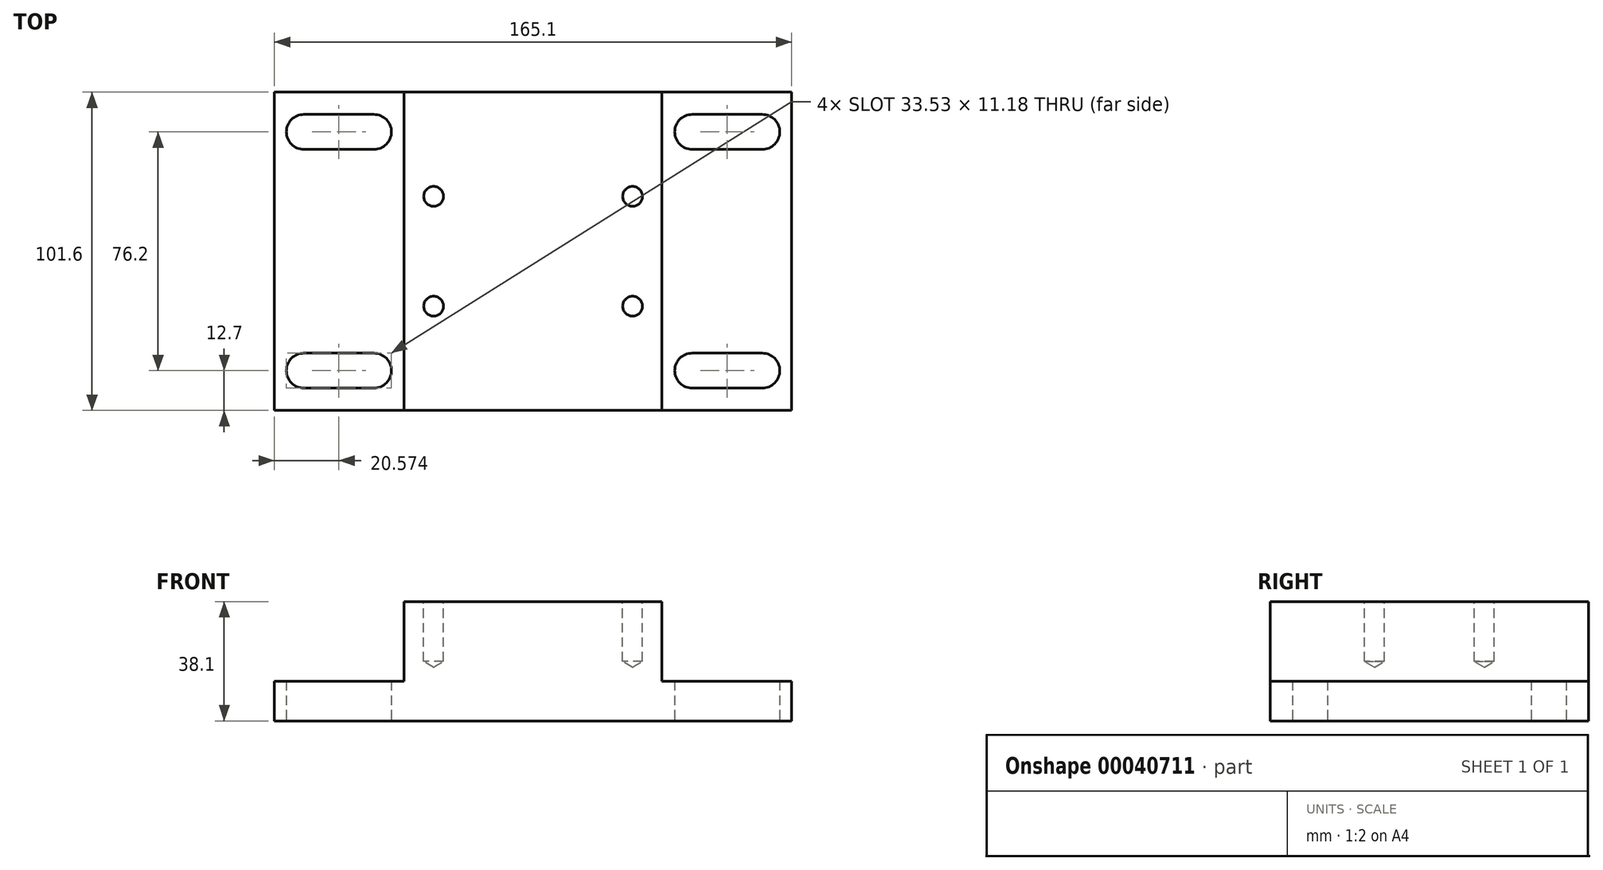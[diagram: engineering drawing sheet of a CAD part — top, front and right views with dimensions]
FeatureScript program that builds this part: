
annotation { "Feature Type Name" : "Feature", "Feature Type Description" : "" }
export const myFeature = defineFeature(function(context is Context, id is Id, definition is map)
    precondition{}
    {
        {
            var Q0;
            Q0=qCreatedBy(makeId("Top.planeOp"),FACE);
            var sketch = newSketch(context, id + "F0", { "sketchPlane" : qUnion([Q0])});
            skLineSegment(sketch, "E0.rect.bottom", {"start": v(-82.55, 50.8) * mm, "end": v(82.55, 50.8) * mm});
            skLineSegment(sketch, "E0.rect.top", {"start": v(-82.55, -50.8) * mm, "end": v(82.55, -50.8) * mm});
            skLineSegment(sketch, "E0.rect.left", {"start": v(-82.55, 50.8) * mm, "end": v(-82.55, -50.8) * mm});
            skLineSegment(sketch, "E0.rect.right", {"start": v(82.55, 50.8) * mm, "end": v(82.55, -50.8) * mm});
            skPoint(sketch, "E0.rect.middle", {"position": v(0, 0) * mm});
            skLineSegment(sketch, "E1", {"start": v(0, 50.8) * mm, "end": v(0, -50.8) * mm, "construction": true});
            skLineSegment(sketch, "E2", {"start": v(-82.55, 0) * mm, "end": v(82.55, 0) * mm, "construction": true});
            skLineSegment(sketch, "E3.0", {"start": v(-82.55, 38.1) * mm, "end": v(82.55, 38.1) * mm, "construction": true});
            skLineSegment(sketch, "E4.0", {"start": v(-61.98, 50.8) * mm, "end": v(-61.98, -50.8) * mm, "construction": true});
            skLineSegment(sketch, "E5.0", {"start": v(-73.15, 50.8) * mm, "end": v(-73.15, -50.8) * mm, "construction": true});
            skLineSegment(sketch, "E6.0", {"start": v(-50.8, 50.8) * mm, "end": v(-50.8, -50.8) * mm, "construction": true});
            skLineSegment(sketch, "E7", {"start": v(-73.15, 38.1) * mm, "end": v(-50.8, 38.1) * mm});
            skArc(sketch, "E8.0.startCap", {"start": v(-73.15, 32.51) * mm, "mid": v(-78.74, 38.1) * mm, "end": v(-73.15, 43.69) * mm});
            skArc(sketch, "E8.0.endCap", {"start": v(-50.8, 43.69) * mm, "mid": v(-45.21, 38.1) * mm, "end": v(-50.8, 32.51) * mm});
            skLineSegment(sketch, "E8.0.left", {"start": v(-73.15, 43.69) * mm, "end": v(-50.8, 43.69) * mm});
            skLineSegment(sketch, "E8.0.right", {"start": v(-73.15, 32.51) * mm, "end": v(-50.8, 32.51) * mm});
            skLineSegment(sketch, "E9.MirrorCS", {"start": v(-73.15, -32.51) * mm, "end": v(-50.8, -32.51) * mm});
            skLineSegment(sketch, "E10.MirrorCS", {"start": v(-73.15, -43.69) * mm, "end": v(-50.8, -43.69) * mm});
            skArc(sketch, "E11.MirrorCS", {"start": v(-50.8, -43.69) * mm, "mid": v(-45.21, -38.1) * mm, "end": v(-50.8, -32.51) * mm});
            skArc(sketch, "E12.MirrorCS", {"start": v(-73.15, -32.51) * mm, "mid": v(-78.74, -38.1) * mm, "end": v(-73.15, -43.69) * mm});
            skLineSegment(sketch, "E13.MirrorCS", {"start": v(-73.15, -38.1) * mm, "end": v(-50.8, -38.1) * mm});
            skArc(sketch, "E14.MirrorCS", {"start": v(50.8, 43.69) * mm, "mid": v(45.21, 38.1) * mm, "end": v(50.8, 32.51) * mm});
            skArc(sketch, "E15.MirrorCS", {"start": v(73.15, 32.51) * mm, "mid": v(78.74, 38.1) * mm, "end": v(73.15, 43.69) * mm});
            skLineSegment(sketch, "E16.MirrorCS", {"start": v(73.15, 38.1) * mm, "end": v(50.8, 38.1) * mm});
            skLineSegment(sketch, "E17.MirrorCS", {"start": v(73.15, 43.69) * mm, "end": v(50.8, 43.69) * mm});
            skLineSegment(sketch, "E18.MirrorCS", {"start": v(73.15, 32.51) * mm, "end": v(50.8, 32.51) * mm});
            skLineSegment(sketch, "E19.MirrorCS", {"start": v(73.15, -43.69) * mm, "end": v(50.8, -43.69) * mm});
            skArc(sketch, "E20.MirrorCS", {"start": v(73.15, -32.51) * mm, "mid": v(78.74, -38.1) * mm, "end": v(73.15, -43.69) * mm});
            skLineSegment(sketch, "E21.MirrorCS", {"start": v(73.15, -38.1) * mm, "end": v(50.8, -38.1) * mm});
            skLineSegment(sketch, "E22.MirrorCS", {"start": v(73.15, -32.51) * mm, "end": v(50.8, -32.51) * mm});
            skArc(sketch, "E23.MirrorCS", {"start": v(50.8, -43.69) * mm, "mid": v(45.21, -38.1) * mm, "end": v(50.8, -32.51) * mm});
            skSolve(sketch);
        }
        {
            var Q0;
            Q0 = qSketchRegion(id + "F0", true);
            extrude(context, id + "F1", {"entities" : qUnion([Q0]), "depth" : 12.7 * mm});
        }
        {
            var Q0;
            Q0=makeQuery(id+"F1.opExtrude","CAP_FACE",FACE,{"disambiguationData":[OSD([sQuery(id+"F0.wireOp",EDGE,"E0.rect.bottom"),sQuery(id+"F0.wireOp",EDGE,"E0.rect.top"),sQuery(id+"F0.wireOp",EDGE,"E0.rect.left"),sQuery(id+"F0.wireOp",EDGE,"E0.rect.right"),sQuery(id+"F0.wireOp",EDGE,"E8.0.startCap"),sQuery(id+"F0.wireOp",EDGE,"E8.0.endCap"),sQuery(id+"F0.wireOp",EDGE,"E8.0.left"),sQuery(id+"F0.wireOp",EDGE,"E8.0.right"),sQuery(id+"F0.wireOp",EDGE,"E9.MirrorCS"),sQuery(id+"F0.wireOp",EDGE,"E10.MirrorCS"),sQuery(id+"F0.wireOp",EDGE,"E11.MirrorCS"),sQuery(id+"F0.wireOp",EDGE,"E12.MirrorCS"),sQuery(id+"F0.wireOp",EDGE,"E14.MirrorCS"),sQuery(id+"F0.wireOp",EDGE,"E15.MirrorCS"),sQuery(id+"F0.wireOp",EDGE,"E17.MirrorCS"),sQuery(id+"F0.wireOp",EDGE,"E18.MirrorCS"),sQuery(id+"F0.wireOp",EDGE,"E19.MirrorCS"),sQuery(id+"F0.wireOp",EDGE,"E20.MirrorCS"),sQuery(id+"F0.wireOp",EDGE,"E22.MirrorCS"),sQuery(id+"F0.wireOp",EDGE,"E23.MirrorCS")])],"isStart":false});
            var sketch = newSketch(context, id + "F2", { "sketchPlane" : qUnion([Q0])});
            skLineSegment(sketch, "E24", {"start": v(0, 50.8) * mm, "end": v(0, -50.8) * mm, "construction": true});
            skLineSegment(sketch, "E25.0", {"start": v(-41.15, 50.8) * mm, "end": v(-41.15, -50.8) * mm, "construction": true});
            skLineSegment(sketch, "E26.bottom", {"start": v(-41.15, 50.8) * mm, "end": v(41.15, 50.8) * mm});
            skLineSegment(sketch, "E26.top", {"start": v(-41.15, -50.8) * mm, "end": v(41.15, -50.8) * mm});
            skLineSegment(sketch, "E26.left", {"start": v(-41.15, 50.8) * mm, "end": v(-41.15, -50.8) * mm});
            skLineSegment(sketch, "E26.right", {"start": v(41.15, 50.8) * mm, "end": v(41.15, -50.8) * mm});
            skSolve(sketch);
        }
        {
            var Q0;
            Q0 = qSketchRegion(id + "F2", true);
            extrude(context, id + "F3", {"entities" : qUnion([Q0]), "operationType" : NewBodyOperationType.ADD, "depth" : 25.4 * mm});
        }
        {
            var Q0;
            Q0=makeQuery(id+"F3.opExtrude","CAP_FACE",FACE,{"disambiguationData":[OSD([sQuery(id+"F2.wireOp",EDGE,"E26.bottom"),sQuery(id+"F2.wireOp",EDGE,"E26.top"),sQuery(id+"F2.wireOp",EDGE,"E26.left"),sQuery(id+"F2.wireOp",EDGE,"E26.right")])],"isStart":false});
            var sketch = newSketch(context, id + "F4", { "sketchPlane" : qUnion([Q0])});
            skLineSegment(sketch, "E27", {"start": v(0, 50.8) * mm, "end": v(0, -50.8) * mm, "construction": true});
            skLineSegment(sketch, "E28", {"start": v(-41.15, 0) * mm, "end": v(41.15, 0) * mm, "construction": true});
            skLineSegment(sketch, "E29.0", {"start": v(-31.75, 50.8) * mm, "end": v(-31.75, -50.8) * mm, "construction": true});
            skLineSegment(sketch, "E30.0", {"start": v(-41.15, 17.53) * mm, "end": v(41.15, 17.53) * mm, "construction": true});
            skPoint(sketch, "E31", {"position": v(-31.75, 17.53) * mm});
            skPoint(sketch, "E32.MirrorP", {"position": v(-31.75, -17.53) * mm});
            skPoint(sketch, "E33.MirrorP", {"position": v(31.75, 17.53) * mm});
            skPoint(sketch, "E34.MirrorP", {"position": v(31.75, -17.53) * mm});
            skSolve(sketch);
        }
        {
            var Q0;
            Q0=sQuery(id+"F4.wireOp",VERTEX,"E31");
            var Q1;
            Q1=sQuery(id+"F4.wireOp",VERTEX,"E32.MirrorP");
            var Q2;
            Q2=sQuery(id+"F4.wireOp",VERTEX,"E34.MirrorP");
            var Q3;
            Q3=sQuery(id+"F4.wireOp",VERTEX,"E33.MirrorP");
            var Q4;
            Q4=makeQuery(id+"F1.opExtrude","SWEPT_BODY",BODY,{"disambiguationData":[OSD([sQuery(id+"F0.wireOp",EDGE,"E0.rect.bottom"),sQuery(id+"F0.wireOp",EDGE,"E0.rect.top"),sQuery(id+"F0.wireOp",EDGE,"E0.rect.left"),sQuery(id+"F0.wireOp",EDGE,"E0.rect.right"),sQuery(id+"F0.wireOp",EDGE,"E8.0.startCap"),sQuery(id+"F0.wireOp",EDGE,"E8.0.endCap"),sQuery(id+"F0.wireOp",EDGE,"E8.0.left"),sQuery(id+"F0.wireOp",EDGE,"E8.0.right"),sQuery(id+"F0.wireOp",EDGE,"E9.MirrorCS"),sQuery(id+"F0.wireOp",EDGE,"E10.MirrorCS"),sQuery(id+"F0.wireOp",EDGE,"E11.MirrorCS"),sQuery(id+"F0.wireOp",EDGE,"E12.MirrorCS"),sQuery(id+"F0.wireOp",EDGE,"E14.MirrorCS"),sQuery(id+"F0.wireOp",EDGE,"E15.MirrorCS"),sQuery(id+"F0.wireOp",EDGE,"E17.MirrorCS"),sQuery(id+"F0.wireOp",EDGE,"E18.MirrorCS"),sQuery(id+"F0.wireOp",EDGE,"E19.MirrorCS"),sQuery(id+"F0.wireOp",EDGE,"E20.MirrorCS"),sQuery(id+"F0.wireOp",EDGE,"E22.MirrorCS"),sQuery(id+"F0.wireOp",EDGE,"E23.MirrorCS")])]});
            hole(context, id + "F5", {"style" : HoleStyle.SIMPLE, "holeDiameter" : 6.35 * mm, "endStyle" : HoleEndStyle.BLIND, "holeDepth" : 19.05 * mm, "locations" : qUnion([Q0, Q1, Q2, Q3]), "scope" : qUnion([Q4])});
        }
    });
